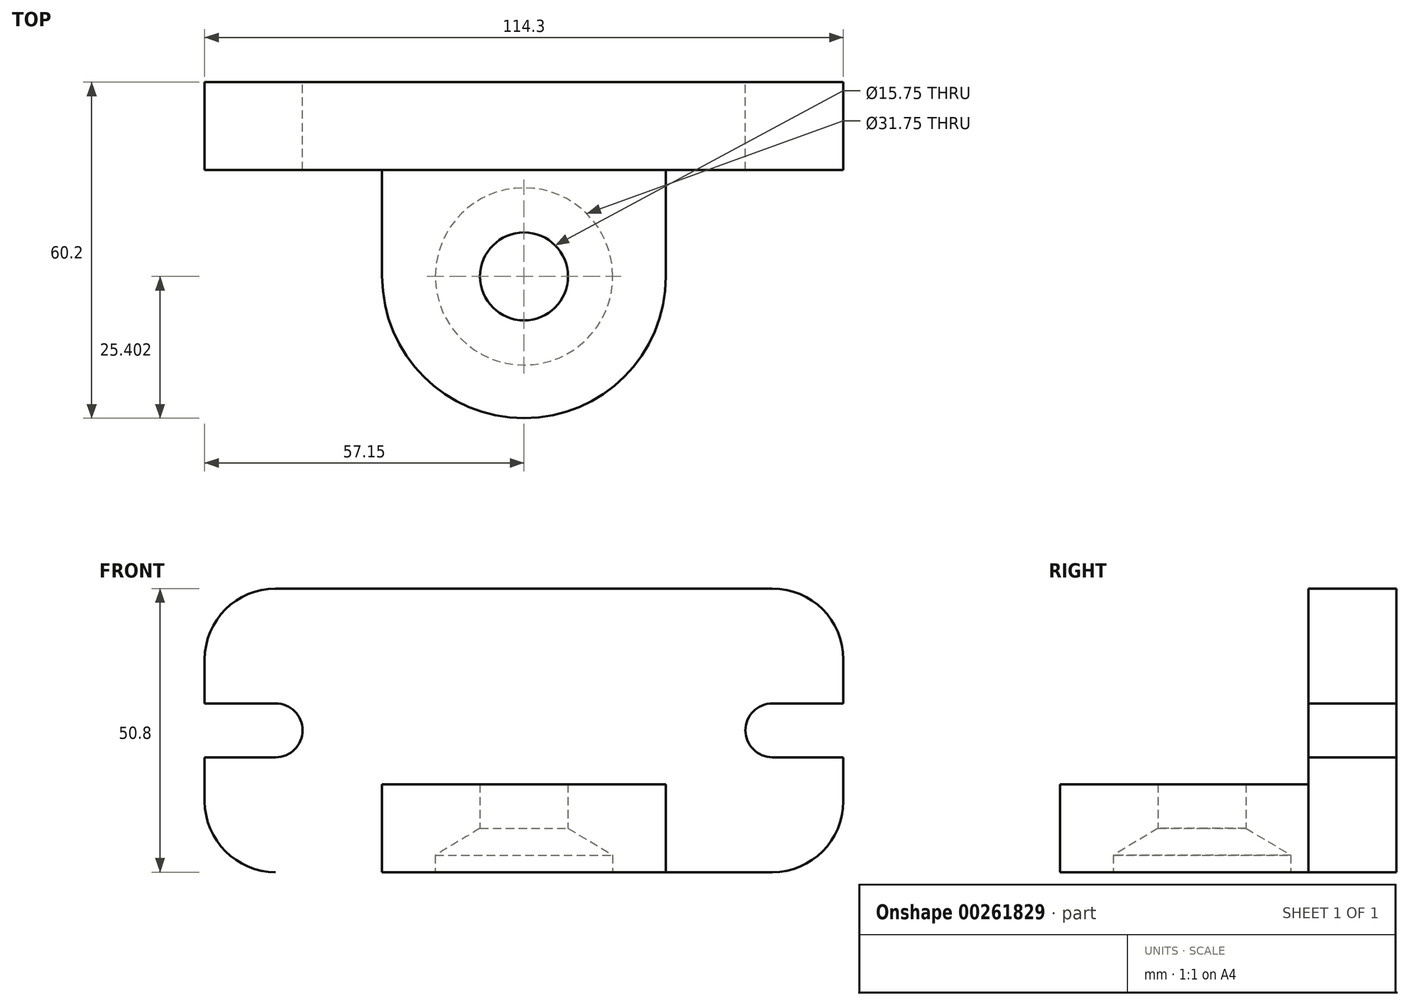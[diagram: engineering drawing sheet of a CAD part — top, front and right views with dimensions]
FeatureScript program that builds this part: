
annotation { "Feature Type Name" : "Feature", "Feature Type Description" : "" }
export const myFeature = defineFeature(function(context is Context, id is Id, definition is map)
    precondition{}
    {
        {
            var Q0;
            Q0=qCreatedBy(makeId("Front.planeOp"),FACE);
            var sketch = newSketch(context, id + "F0", { "sketchPlane" : qUnion([Q0])});
            skLineSegment(sketch, "E0.bottom", {"start": v(-44.45, 25.4) * mm, "end": v(44.45, 25.4) * mm});
            skLineSegment(sketch, "E0.top", {"start": v(-44.45, -25.4) * mm, "end": v(44.45, -25.4) * mm});
            skLineSegment(sketch, "E0.left", {"start": v(-57.15, 12.7) * mm, "end": v(-57.15, 4.83) * mm});
            skLineSegment(sketch, "E0.right", {"start": v(57.15, 12.7) * mm, "end": v(57.15, 4.83) * mm});
            skPoint(sketch, "E1.visualSharp", {"position": v(-57.15, 25.4) * mm});
            skArc(sketch, "E1.filletArc", {"start": v(-44.45, 25.4) * mm, "mid": v(-53.43, 21.68) * mm, "end": v(-57.15, 12.7) * mm});
            skPoint(sketch, "E2.visualSharp", {"position": v(-57.15, -25.4) * mm});
            skArc(sketch, "E2.filletArc", {"start": v(-57.15, -12.7) * mm, "mid": v(-53.43, -21.68) * mm, "end": v(-44.45, -25.4) * mm});
            skPoint(sketch, "E3.visualSharp", {"position": v(57.15, 25.4) * mm});
            skArc(sketch, "E3.filletArc", {"start": v(57.15, 12.7) * mm, "mid": v(53.43, 21.68) * mm, "end": v(44.45, 25.4) * mm});
            skPoint(sketch, "E4.visualSharp", {"position": v(57.15, -25.4) * mm});
            skArc(sketch, "E4.filletArc", {"start": v(44.45, -25.4) * mm, "mid": v(53.43, -21.68) * mm, "end": v(57.15, -12.7) * mm});
            skLineSegment(sketch, "E5.bottom", {"start": v(-57.15, 4.83) * mm, "end": v(-44.45, 4.83) * mm});
            skLineSegment(sketch, "E5.top", {"start": v(-57.15, -4.83) * mm, "end": v(-44.45, -4.83) * mm});
            skArc(sketch, "E6", {"start": v(-44.45, -4.83) * mm, "mid": v(-39.62, 0) * mm, "end": v(-44.45, 4.83) * mm});
            skLineSegment(sketch, "E7.trimOffspring", {"start": v(-57.15, -4.83) * mm, "end": v(-57.15, -12.7) * mm});
            skLineSegment(sketch, "E8.MirrorCS", {"start": v(57.15, 4.83) * mm, "end": v(44.45, 4.83) * mm});
            skArc(sketch, "E9.MirrorCS", {"start": v(44.45, -4.83) * mm, "mid": v(39.62, 0) * mm, "end": v(44.45, 4.83) * mm});
            skLineSegment(sketch, "E10.MirrorCS", {"start": v(57.15, -4.83) * mm, "end": v(44.45, -4.83) * mm});
            skLineSegment(sketch, "E11.trimOffspring", {"start": v(57.15, -4.83) * mm, "end": v(57.15, -12.7) * mm});
            skLineSegment(sketch, "E12.bottom", {"start": v(-25.4, -25.4) * mm, "end": v(25.4, -25.4) * mm});
            skLineSegment(sketch, "E12.top", {"start": v(-25.4, -9.65) * mm, "end": v(25.4, -9.65) * mm});
            skLineSegment(sketch, "E12.left", {"start": v(-25.4, -25.4) * mm, "end": v(-25.4, -9.65) * mm});
            skLineSegment(sketch, "E12.right", {"start": v(25.4, -25.4) * mm, "end": v(25.4, -9.65) * mm});
            skSolve(sketch);
        }
        {
            var Q0;
            Q0 = qSketchRegion(id + "F0", true);
            extrude(context, id + "F1", {"entities" : qUnion([Q0]), "depth" : 15.75 * mm});
        }
        {
            var Q0;
            Q0=makeQuery(id+"F1.opExtrude","SWEPT_FACE",FACE,{"disambiguationData":[OSD([sQuery(id+"F0.wireOp",EDGE,"E0.top"),sQuery(id+"F0.wireOp",EDGE,"E12.bottom")])]});
            var sketch = newSketch(context, id + "F2", { "sketchPlane" : qUnion([Q0])});
            skLineSegment(sketch, "E13.bottom", {"start": v(-25.4, 15.75) * mm, "end": v(25.4, 15.75) * mm});
            skLineSegment(sketch, "E13.left", {"start": v(-25.4, 15.75) * mm, "end": v(-25.4, 37.97) * mm});
            skLineSegment(sketch, "E13.right", {"start": v(25.4, 15.75) * mm, "end": v(25.4, 34.8) * mm});
            skLineSegment(sketch, "E14", {"start": v(-25.4, 34.8) * mm, "end": v(25.4, 34.8) * mm});
            skArc(sketch, "E15", {"start": v(25.4, 34.8) * mm, "mid": v(0, 60.2) * mm, "end": v(-25.4, 34.8) * mm});
            skPoint(sketch, "E15.perimeterSnap0", {"position": v(0, 34.8) * mm});
            skPoint(sketch, "E15.perimeterSnap1", {"position": v(-25.4, 37.97) * mm});
            skPoint(sketch, "E16.orphan", {"position": v(-25.4, 60.2) * mm});
            skPoint(sketch, "E17.orphan", {"position": v(25.4, 60.2) * mm});
            skSolve(sketch);
        }
        {
            var Q0;
            Q0 = qSketchRegion(id + "F2", true);
            extrude(context, id + "F3", {"entities" : qUnion([Q0]), "oppositeDirection" : true, "depth" : 15.75 * mm});
        }
        {
            var Q0;
            Q0=makeQuery(id+"F3.opExtrude","CAP_FACE",FACE,{"disambiguationData":[OSD([sQuery(id+"F2.wireOp",EDGE,"E13.bottom"),sQuery(id+"F2.wireOp",EDGE,"E13.left"),sQuery(id+"F2.wireOp",EDGE,"E13.right"),sQuery(id+"F2.wireOp",EDGE,"E15")])],"isStart":true});
            var sketch = newSketch(context, id + "F4", { "sketchPlane" : qUnion([Q0])});
            skPoint(sketch, "E18.orphan", {"position": v(-25.4, 34.8) * mm});
            skPoint(sketch, "E19.orphan", {"position": v(25.4, 34.8) * mm});
            skPoint(sketch, "E20.center.orphan", {"position": v(0, 34.8) * mm});
            skSolve(sketch);
        }
        {
            var Q0;
            Q0=sQuery(id+"F4.wireOp",VERTEX,"E20.center.orphan");
            var Q1;
            Q1=makeQuery(id+"F3.opExtrude","SWEPT_BODY",BODY,{"disambiguationData":[OSD([sQuery(id+"F2.wireOp",EDGE,"E13.bottom"),sQuery(id+"F2.wireOp",EDGE,"E13.left"),sQuery(id+"F2.wireOp",EDGE,"E13.right"),sQuery(id+"F2.wireOp",EDGE,"E15")])]});
            hole(context, id + "F5", {"style" : HoleStyle.SIMPLE, "endStyle" : HoleEndStyle.THROUGH, "holeDiameter" : 15.75 * mm, "tappedDepth" : 12.7 * mm, "tapClearance" : 3, "locations" : qUnion([Q0]), "scope" : qUnion([Q1])});
        }
        {
            var Q0;
            Q0=makeQuery(id+"F3.opExtrude","CAP_FACE",FACE,{"disambiguationData":[OSD([sQuery(id+"F2.wireOp",EDGE,"E13.bottom"),sQuery(id+"F2.wireOp",EDGE,"E13.left"),sQuery(id+"F2.wireOp",EDGE,"E13.right"),sQuery(id+"F2.wireOp",EDGE,"E15")])],"isStart":true});
            var sketch = newSketch(context, id + "F6", { "sketchPlane" : qUnion([Q0])});
            skPoint(sketch, "E21", {"position": v(0, 34.8) * mm});
            skSolve(sketch);
        }
        {
            var Q0;
            Q0=sQuery(id+"F6.wireOp",VERTEX,"E21");
            var Q1;
            Q1=makeQuery(id+"F3.opExtrude","SWEPT_BODY",BODY,{"disambiguationData":[OSD([sQuery(id+"F2.wireOp",EDGE,"E13.bottom"),sQuery(id+"F2.wireOp",EDGE,"E13.left"),sQuery(id+"F2.wireOp",EDGE,"E13.right"),sQuery(id+"F2.wireOp",EDGE,"E15")])]});
            hole(context, id + "F7", {"style" : HoleStyle.SIMPLE, "endStyle" : HoleEndStyle.BLIND, "holeDiameter" : 31.75 * mm, "holeDepth" : 3.05 * mm, "tappedDepth" : 12.7 * mm, "tapClearance" : 3, "locations" : qUnion([Q0]), "scope" : qUnion([Q1])});
        }
    });
